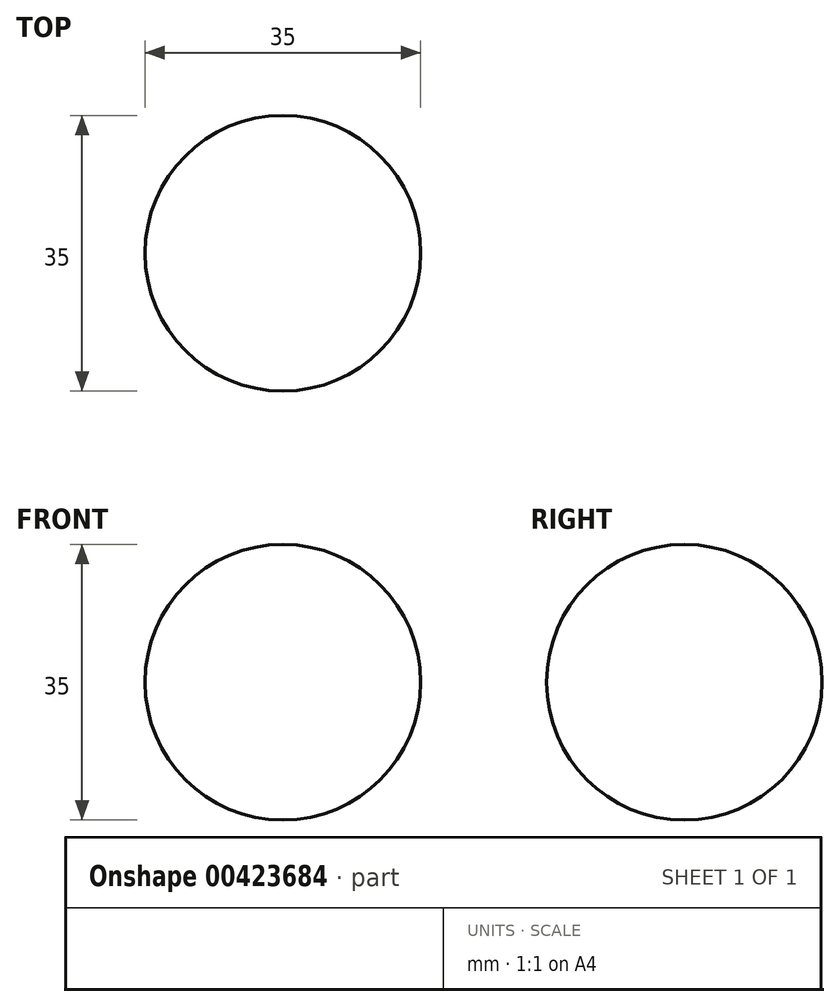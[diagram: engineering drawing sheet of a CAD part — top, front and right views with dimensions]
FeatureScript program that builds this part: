
annotation { "Feature Type Name" : "Feature", "Feature Type Description" : "" }
export const myFeature = defineFeature(function(context is Context, id is Id, definition is map)
    precondition{}
    {
        {
            var Q0;
            Q0=qCreatedBy(makeId("Right.planeOp"),FACE);
            var sketch = newSketch(context, id + "F0", { "sketchPlane" : qUnion([Q0])});
            skLineSegment(sketch, "E0", {"start": v(0, 17.5) * mm, "end": v(0, -17.5) * mm});
            skArc(sketch, "E1", {"start": v(0, 17.5) * mm, "mid": v(-17.5, 0) * mm, "end": v(0, -17.5) * mm});
            skSolve(sketch);
        }
        {
            var Q0;
            Q0=makeQuery(id+"F0.imprint","IMPRINT",FACE,{"disambiguationData":[TD([[makeQuery(id+"F0.imprint","IMPRINT",EDGE,{"derivedFrom":sQuery(id+"F0.wireOp",EDGE,"E0")}),-1.0]])]});
            var Q1;
            Q1=sQuery(id+"F0.wireOp",EDGE,"E0");
            revolve(context, id + "F1", {"entities" : qUnion([Q0]), "axis" : qUnion([Q1]), "revolveType" : RevolveType.FULL});
        }
    });
